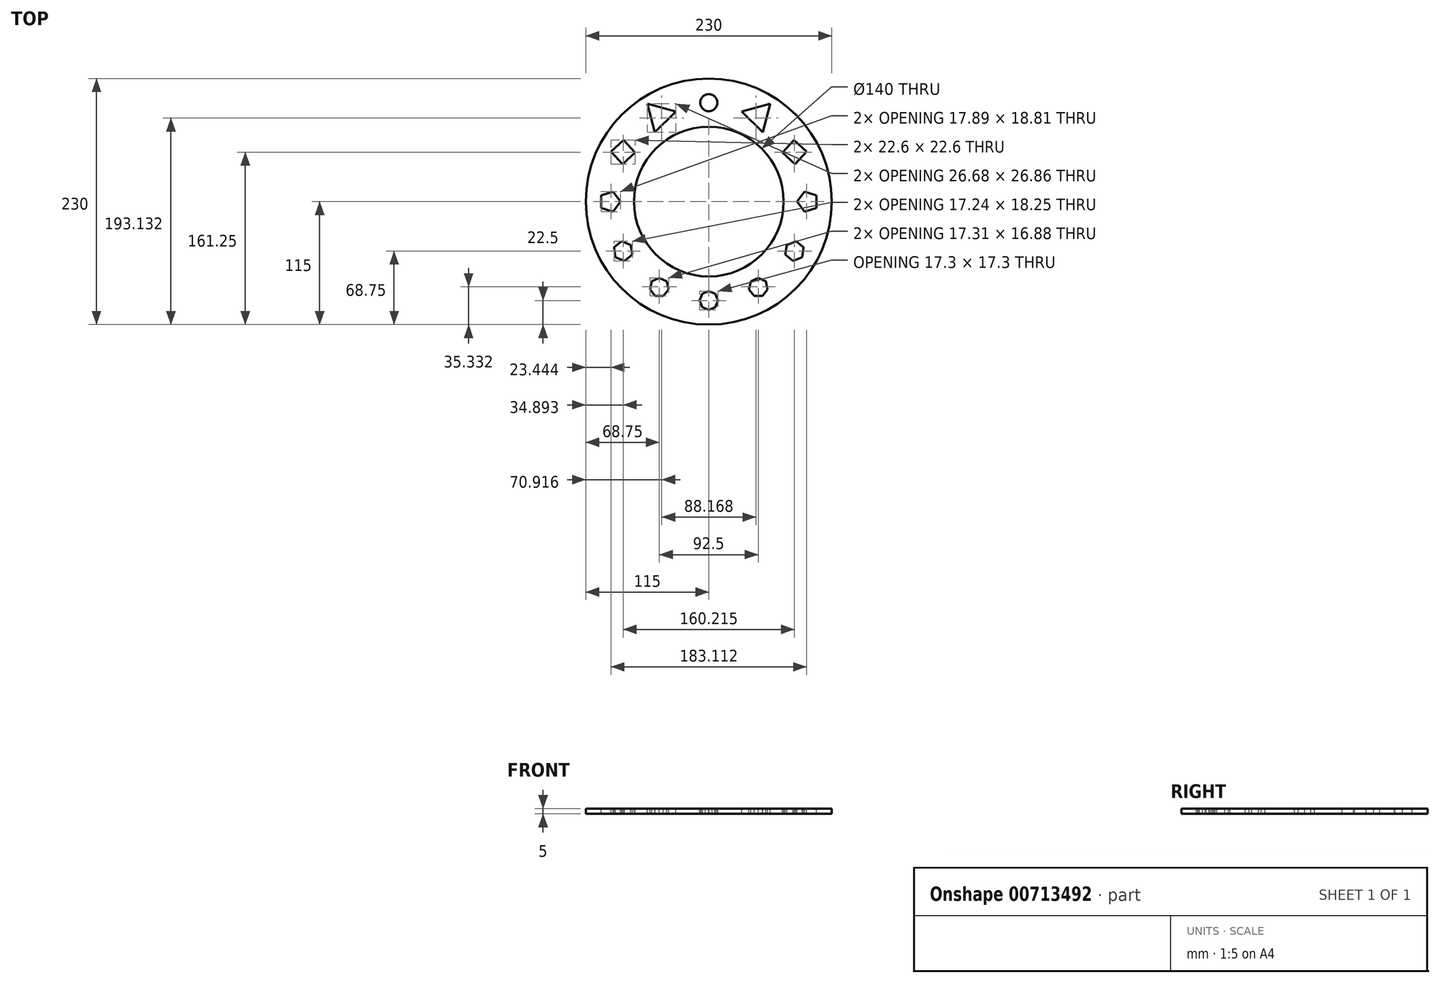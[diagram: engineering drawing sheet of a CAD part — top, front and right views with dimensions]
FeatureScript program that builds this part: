
annotation { "Feature Type Name" : "Feature", "Feature Type Description" : "" }
export const myFeature = defineFeature(function(context is Context, id is Id, definition is map)
    precondition{}
    {
        {
            var Q0;
            Q0=qCreatedBy(makeId("Top.planeOp"),FACE);
            var sketch = newSketch(context, id + "F0", { "sketchPlane" : qUnion([Q0])});
            skCircle(sketch, "E0", {"center": v(0, 0) * mm, "radius": 70 * mm});
            skCircle(sketch, "E1", {"center": v(0, 0) * mm, "radius": 115 * mm});
            skSolve(sketch);
        }
        {
            var Q0;
            Q0=makeQuery(id+"F0.imprint","IMPRINT",FACE,{"disambiguationData":[TD([[makeQuery(id+"F0.imprint","IMPRINT",EDGE,{"derivedFrom":sQuery(id+"F0.wireOp",EDGE,"E0")}),-1.0]])]});
            extrude(context, id + "F1", {"entities" : qUnion([Q0]), "depth" : 5 * mm, "offsetDistance" : 25 * mm});
        }
        {
            var Q0;
            Q0=makeQuery(id+"F1.opExtrude","CAP_FACE",FACE,{"disambiguationData":[OSD([sQuery(id+"F0.wireOp",EDGE,"E0"),sQuery(id+"F0.wireOp",EDGE,"E1")])],"isStart":false});
            var sketch = newSketch(context, id + "F2", { "sketchPlane" : qUnion([Q0])});
            skCircle(sketch, "E2", {"center": v(0, 92.5) * mm, "radius": 8 * mm});
            skLineSegment(sketch, "E3", {"start": v(0, 92.5) * mm, "end": v(0, 0) * mm, "construction": true});
            skLineSegment(sketch, "E4", {"start": v(0, 0) * mm, "end": v(46.25, 80.1) * mm});
            skCircle(sketch, "E5.cCircle", {"center": v(46.25, 80.1) * mm, "radius": 8 * mm, "construction": true});
            skLineSegment(sketch, "E5.0", {"start": v(30.75, 84.06) * mm, "end": v(57.42, 91.56) * mm});
            skLineSegment(sketch, "E5.1", {"start": v(57.42, 91.56) * mm, "end": v(50.58, 64.7) * mm});
            skLineSegment(sketch, "E5.2", {"start": v(50.58, 64.7) * mm, "end": v(30.75, 84.06) * mm});
            skPoint(sketch, "E5.0.midPoint", {"position": v(44.08, 87.8) * mm});
            skCircle(sketch, "E6.cCircle", {"center": v(80.1, 46.25) * mm, "radius": 8 * mm, "construction": true});
            skLineSegment(sketch, "E6.0", {"start": v(91.4, 46.8) * mm, "end": v(80.66, 34.95) * mm});
            skLineSegment(sketch, "E6.1", {"start": v(80.66, 34.95) * mm, "end": v(68.8, 45.7) * mm});
            skLineSegment(sketch, "E6.2", {"start": v(68.8, 45.7) * mm, "end": v(79.55, 57.55) * mm});
            skLineSegment(sketch, "E6.3", {"start": v(79.55, 57.55) * mm, "end": v(91.4, 46.8) * mm});
            skPoint(sketch, "E6.0.midPoint", {"position": v(86.04, 40.88) * mm});
            skLineSegment(sketch, "E7", {"start": v(80.1, 46.25) * mm, "end": v(0, 0) * mm});
            skCircle(sketch, "E8.cCircle", {"center": v(92.5, 0) * mm, "radius": 8 * mm, "construction": true});
            skLineSegment(sketch, "E8.0", {"start": v(100.5, 5.81) * mm, "end": v(100.5, -5.81) * mm});
            skLineSegment(sketch, "E8.1", {"start": v(100.5, -5.81) * mm, "end": v(89.44, -9.4) * mm});
            skLineSegment(sketch, "E8.2", {"start": v(89.44, -9.4) * mm, "end": v(82.61, 0) * mm});
            skLineSegment(sketch, "E8.3", {"start": v(82.61, 0) * mm, "end": v(89.44, 9.4) * mm});
            skLineSegment(sketch, "E8.4", {"start": v(89.44, 9.4) * mm, "end": v(100.5, 5.81) * mm});
            skPoint(sketch, "E8.0.midPoint", {"position": v(100.5, 0) * mm});
            skCircle(sketch, "E9.cCircle", {"center": v(80.1, -46.25) * mm, "radius": 8 * mm, "construction": true});
            skLineSegment(sketch, "E9.0", {"start": v(87.3, -52.06) * mm, "end": v(78.67, -55.37) * mm});
            skLineSegment(sketch, "E9.1", {"start": v(78.67, -55.37) * mm, "end": v(71.49, -49.57) * mm});
            skLineSegment(sketch, "E9.2", {"start": v(71.49, -49.57) * mm, "end": v(72.92, -40.44) * mm});
            skLineSegment(sketch, "E9.3", {"start": v(72.92, -40.44) * mm, "end": v(81.55, -37.13) * mm});
            skLineSegment(sketch, "E9.4", {"start": v(81.55, -37.13) * mm, "end": v(88.73, -42.93) * mm});
            skLineSegment(sketch, "E9.5", {"start": v(88.73, -42.93) * mm, "end": v(87.3, -52.06) * mm});
            skPoint(sketch, "E9.0.midPoint", {"position": v(82.98, -53.72) * mm});
            skCircle(sketch, "E10.cCircle", {"center": v(46.25, -80.1) * mm, "radius": 8 * mm, "construction": true});
            skLineSegment(sketch, "E10.0", {"start": v(50.1, -88.1) * mm, "end": v(42.4, -88.1) * mm});
            skLineSegment(sketch, "E10.1", {"start": v(42.4, -88.1) * mm, "end": v(37.6, -82.08) * mm});
            skLineSegment(sketch, "E10.2", {"start": v(37.6, -82.08) * mm, "end": v(39.3, -74.57) * mm});
            skLineSegment(sketch, "E10.3", {"start": v(39.3, -74.57) * mm, "end": v(46.25, -71.23) * mm});
            skLineSegment(sketch, "E10.4", {"start": v(46.25, -71.23) * mm, "end": v(53.2, -74.57) * mm});
            skLineSegment(sketch, "E10.5", {"start": v(53.2, -74.57) * mm, "end": v(54.9, -82.08) * mm});
            skLineSegment(sketch, "E10.6", {"start": v(54.9, -82.08) * mm, "end": v(50.1, -88.1) * mm});
            skPoint(sketch, "E10.0.midPoint", {"position": v(46.25, -88.1) * mm});
            skCircle(sketch, "E11.cCircle", {"center": v(0, -92.5) * mm, "radius": 8 * mm, "construction": true});
            skLineSegment(sketch, "E11.0", {"start": v(5.82, -98.9) * mm, "end": v(-0.42, -101.15) * mm});
            skLineSegment(sketch, "E11.1", {"start": v(-0.42, -101.15) * mm, "end": v(-6.4, -98.32) * mm});
            skLineSegment(sketch, "E11.2", {"start": v(-6.4, -98.32) * mm, "end": v(-8.65, -92.08) * mm});
            skLineSegment(sketch, "E11.3", {"start": v(-8.65, -92.08) * mm, "end": v(-5.82, -86.1) * mm});
            skLineSegment(sketch, "E11.4", {"start": v(-5.82, -86.1) * mm, "end": v(0.42, -83.85) * mm});
            skLineSegment(sketch, "E11.5", {"start": v(0.42, -83.85) * mm, "end": v(6.4, -86.68) * mm});
            skLineSegment(sketch, "E11.6", {"start": v(6.4, -86.68) * mm, "end": v(8.65, -92.92) * mm});
            skLineSegment(sketch, "E11.7", {"start": v(8.65, -92.92) * mm, "end": v(5.82, -98.9) * mm});
            skPoint(sketch, "E11.0.midPoint", {"position": v(2.7, -100.03) * mm});
            skLineSegment(sketch, "E12", {"start": v(0, 0) * mm, "end": v(92.5, 0) * mm, "construction": true});
            skLineSegment(sketch, "E13", {"start": v(80.1, -46.25) * mm, "end": v(0, 0) * mm, "construction": true});
            skLineSegment(sketch, "E14", {"start": v(46.25, -80.1) * mm, "end": v(0, 0) * mm, "construction": true});
            skLineSegment(sketch, "E15", {"start": v(0, -92.5) * mm, "end": v(0, 0) * mm, "construction": true});
            skLineSegment(sketch, "E16.MirrorCS", {"start": v(-50.58, 64.7) * mm, "end": v(-30.75, 84.06) * mm});
            skLineSegment(sketch, "E17.MirrorCS", {"start": v(-30.75, 84.06) * mm, "end": v(-57.42, 91.56) * mm});
            skLineSegment(sketch, "E18.MirrorCS", {"start": v(-57.42, 91.56) * mm, "end": v(-50.58, 64.7) * mm});
            skLineSegment(sketch, "E19.MirrorCS", {"start": v(-68.8, 45.7) * mm, "end": v(-79.55, 57.55) * mm});
            skLineSegment(sketch, "E20.MirrorCS", {"start": v(-79.55, 57.55) * mm, "end": v(-91.4, 46.8) * mm});
            skLineSegment(sketch, "E21.MirrorCS", {"start": v(-80.66, 34.95) * mm, "end": v(-68.8, 45.7) * mm});
            skLineSegment(sketch, "E22.MirrorCS", {"start": v(-91.4, 46.8) * mm, "end": v(-80.66, 34.95) * mm});
            skLineSegment(sketch, "E23.MirrorCS", {"start": v(-89.44, -9.4) * mm, "end": v(-82.61, 0) * mm});
            skLineSegment(sketch, "E24.MirrorCS", {"start": v(-82.61, 0) * mm, "end": v(-89.44, 9.4) * mm});
            skLineSegment(sketch, "E25.MirrorCS", {"start": v(-89.44, 9.4) * mm, "end": v(-100.5, 5.81) * mm});
            skLineSegment(sketch, "E26.MirrorCS", {"start": v(-100.5, -5.81) * mm, "end": v(-89.44, -9.4) * mm});
            skLineSegment(sketch, "E27.MirrorCS", {"start": v(-100.5, 5.81) * mm, "end": v(-100.5, -5.81) * mm});
            skLineSegment(sketch, "E28.MirrorCS", {"start": v(-72.92, -40.44) * mm, "end": v(-81.55, -37.13) * mm});
            skCircle(sketch, "E29.MirrorC", {"center": v(-80.1, -46.25) * mm, "radius": 8 * mm, "construction": true});
            skLineSegment(sketch, "E30.MirrorCS", {"start": v(-71.49, -49.57) * mm, "end": v(-72.92, -40.44) * mm});
            skPoint(sketch, "E31.MirrorP", {"position": v(-82.98, -53.72) * mm});
            skLineSegment(sketch, "E32.MirrorCS", {"start": v(-78.67, -55.37) * mm, "end": v(-71.49, -49.57) * mm});
            skLineSegment(sketch, "E33.MirrorCS", {"start": v(-80.1, -46.25) * mm, "end": v(0, 0) * mm, "construction": true});
            skLineSegment(sketch, "E34.MirrorCS", {"start": v(-81.55, -37.13) * mm, "end": v(-88.73, -42.93) * mm});
            skLineSegment(sketch, "E35.MirrorCS", {"start": v(-88.73, -42.93) * mm, "end": v(-87.3, -52.06) * mm});
            skLineSegment(sketch, "E36.MirrorCS", {"start": v(-87.3, -52.06) * mm, "end": v(-78.67, -55.37) * mm});
            skLineSegment(sketch, "E37.MirrorCS", {"start": v(-42.4, -88.1) * mm, "end": v(-37.6, -82.08) * mm});
            skLineSegment(sketch, "E38.MirrorCS", {"start": v(-39.3, -74.57) * mm, "end": v(-46.25, -71.23) * mm});
            skLineSegment(sketch, "E39.MirrorCS", {"start": v(-54.9, -82.08) * mm, "end": v(-50.1, -88.1) * mm});
            skLineSegment(sketch, "E40.MirrorCS", {"start": v(-50.1, -88.1) * mm, "end": v(-42.4, -88.1) * mm});
            skLineSegment(sketch, "E41.MirrorCS", {"start": v(-37.6, -82.08) * mm, "end": v(-39.3, -74.57) * mm});
            skLineSegment(sketch, "E42.MirrorCS", {"start": v(-53.2, -74.57) * mm, "end": v(-54.9, -82.08) * mm});
            skLineSegment(sketch, "E43.MirrorCS", {"start": v(-46.25, -71.23) * mm, "end": v(-53.2, -74.57) * mm});
            skCircle(sketch, "E44.MirrorC", {"center": v(-46.25, -80.1) * mm, "radius": 8 * mm, "construction": true});
            skPoint(sketch, "E45.MirrorP", {"position": v(-46.25, -88.1) * mm});
            skLineSegment(sketch, "E46.MirrorCS", {"start": v(-46.25, -80.1) * mm, "end": v(0, 0) * mm, "construction": true});
            skLineSegment(sketch, "E47.MirrorCS", {"start": v(-5.82, -98.9) * mm, "end": v(0.42, -101.15) * mm});
            skLineSegment(sketch, "E48.MirrorCS", {"start": v(0.42, -101.15) * mm, "end": v(6.4, -98.32) * mm});
            skLineSegment(sketch, "E49.MirrorCS", {"start": v(-8.65, -92.92) * mm, "end": v(-5.82, -98.9) * mm});
            skLineSegment(sketch, "E50.MirrorCS", {"start": v(5.82, -86.1) * mm, "end": v(-0.42, -83.85) * mm});
            skLineSegment(sketch, "E51.MirrorCS", {"start": v(-6.4, -86.68) * mm, "end": v(-8.65, -92.92) * mm});
            skLineSegment(sketch, "E52.MirrorCS", {"start": v(6.4, -98.32) * mm, "end": v(8.65, -92.08) * mm});
            skLineSegment(sketch, "E53.MirrorCS", {"start": v(8.65, -92.08) * mm, "end": v(5.82, -86.1) * mm});
            skLineSegment(sketch, "E54.MirrorCS", {"start": v(-0.42, -83.85) * mm, "end": v(-6.4, -86.68) * mm});
            skPoint(sketch, "E55.MirrorP", {"position": v(-2.7, -100.03) * mm});
            skSolve(sketch);
        }
        {
            var Q0;
            Q0 = qSketchRegion(id + "F2", true);
            extrude(context, id + "F3", {"entities" : qUnion([Q0]), "operationType" : NewBodyOperationType.REMOVE, "oppositeDirection" : true, "depth" : 25 * mm, "offsetDistance" : 25 * mm});
        }
    });
